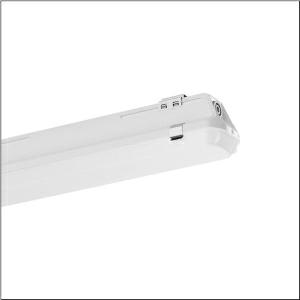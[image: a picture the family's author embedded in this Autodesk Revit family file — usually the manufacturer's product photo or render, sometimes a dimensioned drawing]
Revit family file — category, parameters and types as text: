
# Revit family: monsun_r__21_emergency_51fb20dp467b3h_0bb8
name_source: partatom
category: Lighting Fixtures
units: mm (PartAtom-declared; Revit-internal decimal feet)

## family parameters
Cut with Voids When Loaded = No
Host = Face
Light Source = No
Part Type = Normal
Room Calculation Point = No
Round Connector Dimension = Use Diameter
Shared = No

## types (1)
- --- (1 x LED, 5460 lm, 42.2 W, 4000K)
    Apparent Load = 42 VA
    CIE Flux Codes = 45 75 93 94 100
    Color Rendering = 80
    Color Temperature = 4000K
    Default Elevation = 1800 mm
    Description = Monsun® 21 emergency, damp-proof luminaire, chain hanger, primary optical cover: enclosure, of PC, light emission: direct distribution, primary light characteristic: symmetric, installation type: vertical mounting, horizontal mounting, surface-mounted, suspended mounting, LED, rated luminous flux: 5.460lm, luminous efficacy: 129lm/W, light colour: 840, colour temperature: 4000K, control gear: ECG DALI, with terminal, 5+3-pole, max. 2.5mm², mains connection: 220..240V, AC, 50/60Hz, rated input power: 42W, control gear: single battery element, battery: NiCd, 4,5Ah, mains connection: 230V, housing, of glass-fibre reinforced polyester, uncoated, bright grey, incl. chain hanger, length: 1.590mm, width: 90mm, height: 88mm, clip for enclosure, of stainless steel (V2A), ceiling mounting element, of stainless steel (V2A), chain hanger, of stainless steel (V2A), protection rating (complete): IP66, insulation class (complete): insulation class I (protective earthing), certification: CE, UKCA, protection symbol: D, impact resistance: IK08, permissible operating ambient temperature: +5..+25°C, standard: EN 60598-2-1, EN 50419, EN 60598-2-22, corresponds to IFS (International Featured Standards) requirements for safety and quality in the food industry, for indoor or canopied outdoor use, no direct snow, no direct sun, no direct rain, contact your sales advisor before using the luminaires in applications with unclear chemical exposure, large temperature fluctuations or condensation-forming humidity, LABS conformity tested according to VDMA 24364:2018-05, packaging unit: 1 piece
    Height = 89 mm
    Lamp = 1 x LED
    Lamp Light Flux = 5460 lm
    Lamp Power = 42.2 W
    Lamp count = 1
    Length = 1590 mm
    Luminous efficacy = 129 lm/W
    Manufacturer = Siteco
    ModVariant = No
    Model = 51FB20DP467B3H
    Mounting Place = Ceiling
    Mounting Type = Surface mounted
    Number of Poles = 1
    OnlyDefault = Yes
    Power Factor = 1
    Product Name = Monsun® 21 emergency
    Product group = damp-proof luminaire
    ProductGroupID = 300
    Protection Class = Protection class I
    Protection Degree = IP 66
    RLX_Detail_Level = 1
    RLX_Emergency_Light_Flux = 0 lm
    RLX_Emergency_Type = 0
    RLX_Emergency_Type_DB = No
    RlxData = <blob elided: 92869 chars, md5=2fb84006>
    Socket = socket
    Standby Power = 0 W
    System Light Flux = 5460 lm
    System Power = 42 W
    Type Comments = factory setting: luminous flux: 100 % | dim-lin: 254 | 261 mA
    Type Image = l_1006717.jpg
    URL = http://relux.com
    VarID = @adj_134041
    Voltage = 0 V
    Weight = 0.00 kg
    Width = 90 mm

## geometry (parser evidence)
native form markers: Blend x4, Sweep x13
no freeform markers — native parametric forms only
